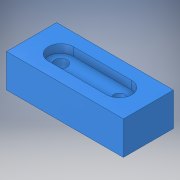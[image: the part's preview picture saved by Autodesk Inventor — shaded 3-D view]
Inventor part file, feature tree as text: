
AUTODESK INVENTOR PART (.ipt)
format: ipt  version: 2018 (Build 220112000, 112)  size: 138,240 bytes
history: native  units: in
note: dims shown in document units (in); Inventor stores cm internally (conversion verified against a paired STEP export)
features: extrude x4, sketch x3, projected_geometry x2
ambient origin geometry x8: Origin, YZ Plane, XZ Plane, XY Plane, X Axis, Y Axis, Z Axis, Center Point
bodies: Body1 (feature_tree)
feature tree (9):
  extrude  "Extrusion5"  Depth=3.5in
  sketch  "Sketch10"  dims[d20=0.3125in d21=1.0in]
  extrude  "Extrusion8"  Depth=1.0in
  extrude  "Extrusion9"  Depth=0.875in
  extrude  "Extrusion10"  Depth=1.0in TaperAngle=0.0deg
  sketch  "Sketch1"  dims[d3=1.5in d4=3.5in]
  projected_geometry  "Projected Loop7"
  sketch  "Sketch12"  dims[d22=0.875in d23=0.875in d24=1.0in d25=0.0in d38=0.38in d39=0.75in d40=0.0in d41=0.75in d42=0.25in d43=0.0in d44=0.5in d45=0.0in]
  projected_geometry  "Projected Loop8"
